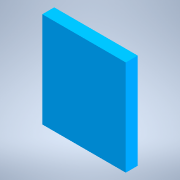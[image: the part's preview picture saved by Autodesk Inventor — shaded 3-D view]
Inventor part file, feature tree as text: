
AUTODESK INVENTOR PART (.ipt)
format: ipt  version: 2022.3 (Build 263350000, 350)  size: 99,328 bytes
history: native  units: in
note: dims shown in document units (in); Inventor stores cm internally (conversion verified against a paired STEP export)
features: extrude x1, sketch x1
ambient origin geometry x8: Origin, YZ Plane, XZ Plane, XY Plane, X Axis, Y Axis, Z Axis, Center Point
bodies: Solid1 (feature_tree)
feature tree (2):
  extrude  "Extrusion1"  Depth=0.8in
  sketch  "Sketch1"  dims[d0=0.7in d1=0.8in d2=0.1in d3=0.0in]
